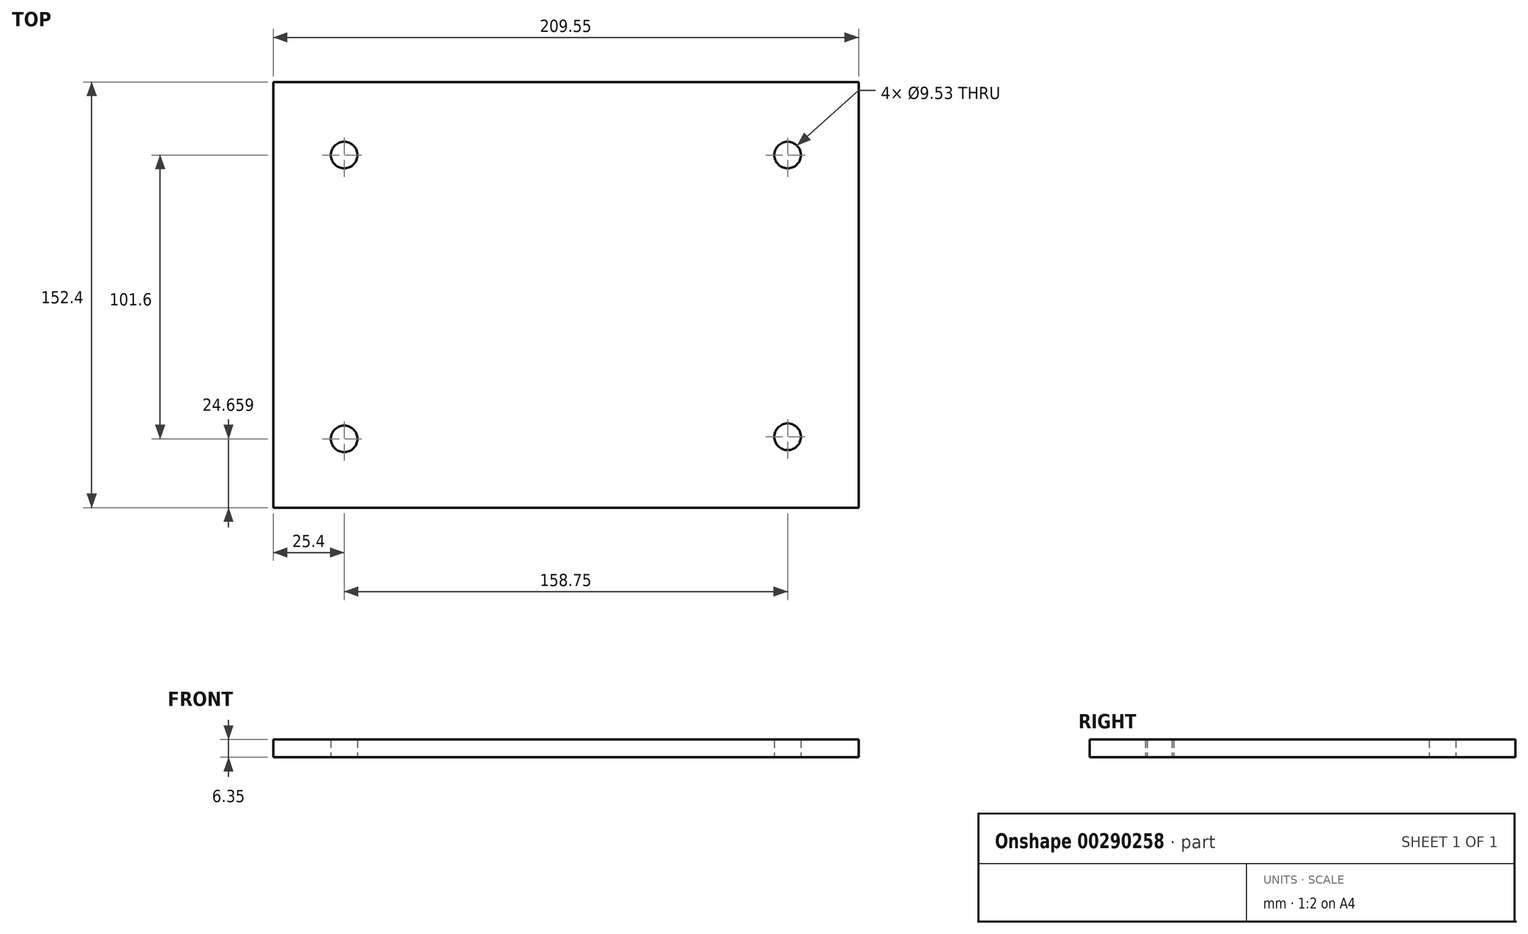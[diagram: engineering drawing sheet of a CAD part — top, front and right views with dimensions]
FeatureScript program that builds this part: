
annotation { "Feature Type Name" : "Feature", "Feature Type Description" : "" }
export const myFeature = defineFeature(function(context is Context, id is Id, definition is map)
    precondition{}
    {
        {
            var Q0;
            Q0=qCreatedBy(makeId("Top.planeOp"),FACE);
            var sketch = newSketch(context, id + "F0", { "sketchPlane" : qUnion([Q0])});
            skLineSegment(sketch, "E0.bottom", {"start": v(0, 0) * mm, "end": v(209.55, 0) * mm});
            skLineSegment(sketch, "E0.top", {"start": v(0, -152.4) * mm, "end": v(209.55, -152.4) * mm});
            skLineSegment(sketch, "E0.left", {"start": v(0, 0) * mm, "end": v(0, -152.4) * mm});
            skLineSegment(sketch, "E0.right", {"start": v(209.55, 0) * mm, "end": v(209.55, -152.4) * mm});
            skCircle(sketch, "E1", {"center": v(25.4, -26.14) * mm, "radius": 4.76 * mm});
            skCircle(sketch, "E2.0.1.0", {"center": v(25.4, -127.74) * mm, "radius": 4.76 * mm});
            skCircle(sketch, "E2.1.0.0", {"center": v(184.15, -26.14) * mm, "radius": 4.76 * mm});
            skCircle(sketch, "E2.1.1.0", {"center": v(184.15, -127) * mm, "radius": 4.76 * mm});
            skLineSegment(sketch, "E2.direction2", {"start": v(25.4, -26.14) * mm, "end": v(25.4, -127.74) * mm, "construction": true});
            skSolve(sketch);
        }
        {
            var Q0;
            Q0=makeQuery(id+"F0.imprint","IMPRINT",FACE,{"disambiguationData":[TD([[makeQuery(id+"F0.imprint","IMPRINT",EDGE,{"derivedFrom":sQuery(id+"F0.wireOp",EDGE,"E0.bottom")}),-1.0]])]});
            extrude(context, id + "F1", {"entities" : qUnion([Q0]), "depth" : 6.35 * mm});
        }
    });
